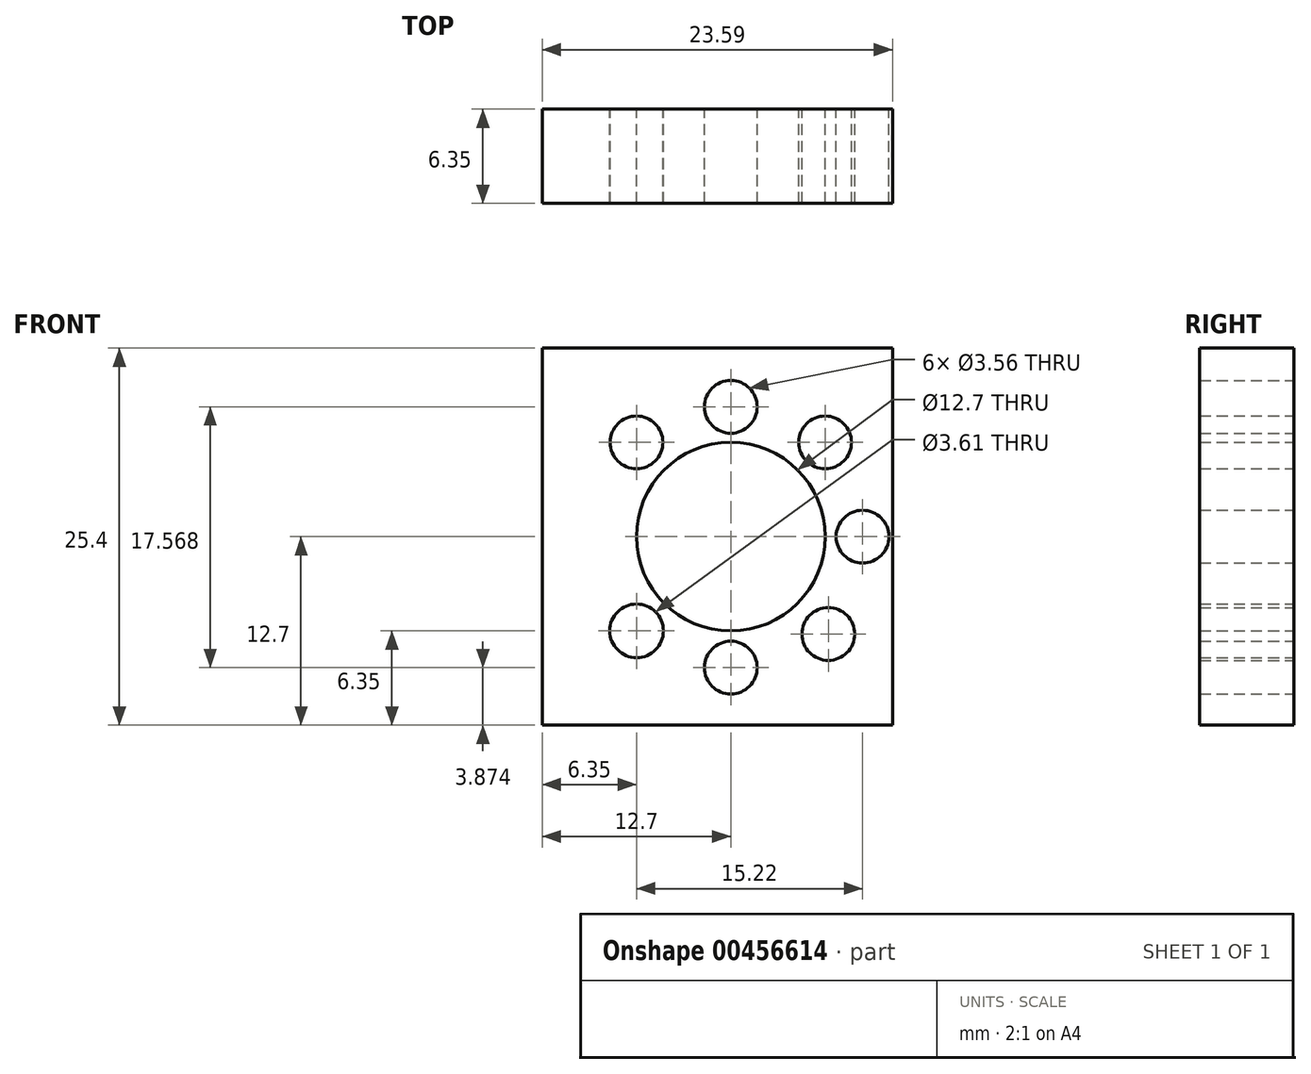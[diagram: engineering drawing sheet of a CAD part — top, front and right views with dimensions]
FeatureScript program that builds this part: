
annotation { "Feature Type Name" : "Feature", "Feature Type Description" : "" }
export const myFeature = defineFeature(function(context is Context, id is Id, definition is map)
    precondition{}
    {
        {
            var Q0;
            Q0=qCreatedBy(makeId("Front.planeOp"),FACE);
            var sketch = newSketch(context, id + "F0", { "sketchPlane" : qUnion([Q0])});
            skCircle(sketch, "E0", {"center": v(0, 0) * mm, "radius": 6.35 * mm});
            skLineSegment(sketch, "E1.right", {"start": v(-12.7, 12.7) * mm, "end": v(-12.7, -12.7) * mm});
            skCircle(sketch, "E2", {"center": v(8.87, 0) * mm, "radius": 1.78 * mm});
            skCircle(sketch, "E3", {"center": v(6.35, 6.35) * mm, "radius": 1.78 * mm});
            skCircle(sketch, "E4", {"center": v(0, 8.74) * mm, "radius": 1.78 * mm});
            skCircle(sketch, "E5", {"center": v(-6.35, 6.35) * mm, "radius": 1.78 * mm});
            skCircle(sketch, "E6", {"center": v(0, -8.83) * mm, "radius": 1.78 * mm});
            skCircle(sketch, "E7", {"center": v(6.56, -6.56) * mm, "radius": 1.78 * mm});
            skCircle(sketch, "E8", {"center": v(-6.35, -6.35) * mm, "radius": 1.8 * mm});
            skLineSegment(sketch, "E9", {"start": v(-12.7, 12.7) * mm, "end": v(10.65, 12.7) * mm});
            skLineSegment(sketch, "E10", {"start": v(-12.7, -12.7) * mm, "end": v(10.65, -12.7) * mm});
            skLineSegment(sketch, "E11", {"start": v(10.65, 12.7) * mm, "end": v(10.89, 12.7) * mm});
            skLineSegment(sketch, "E12", {"start": v(10.89, 12.7) * mm, "end": v(10.89, -12.7) * mm});
            skLineSegment(sketch, "E13", {"start": v(10.65, -12.7) * mm, "end": v(10.89, -12.7) * mm});
            skSolve(sketch);
        }
        {
            var Q0;
            Q0 = qSketchRegion(id + "F0", true);
            extrude(context, id + "F1", {"entities" : qUnion([Q0]), "depth" : 6.35 * mm});
        }
    });
